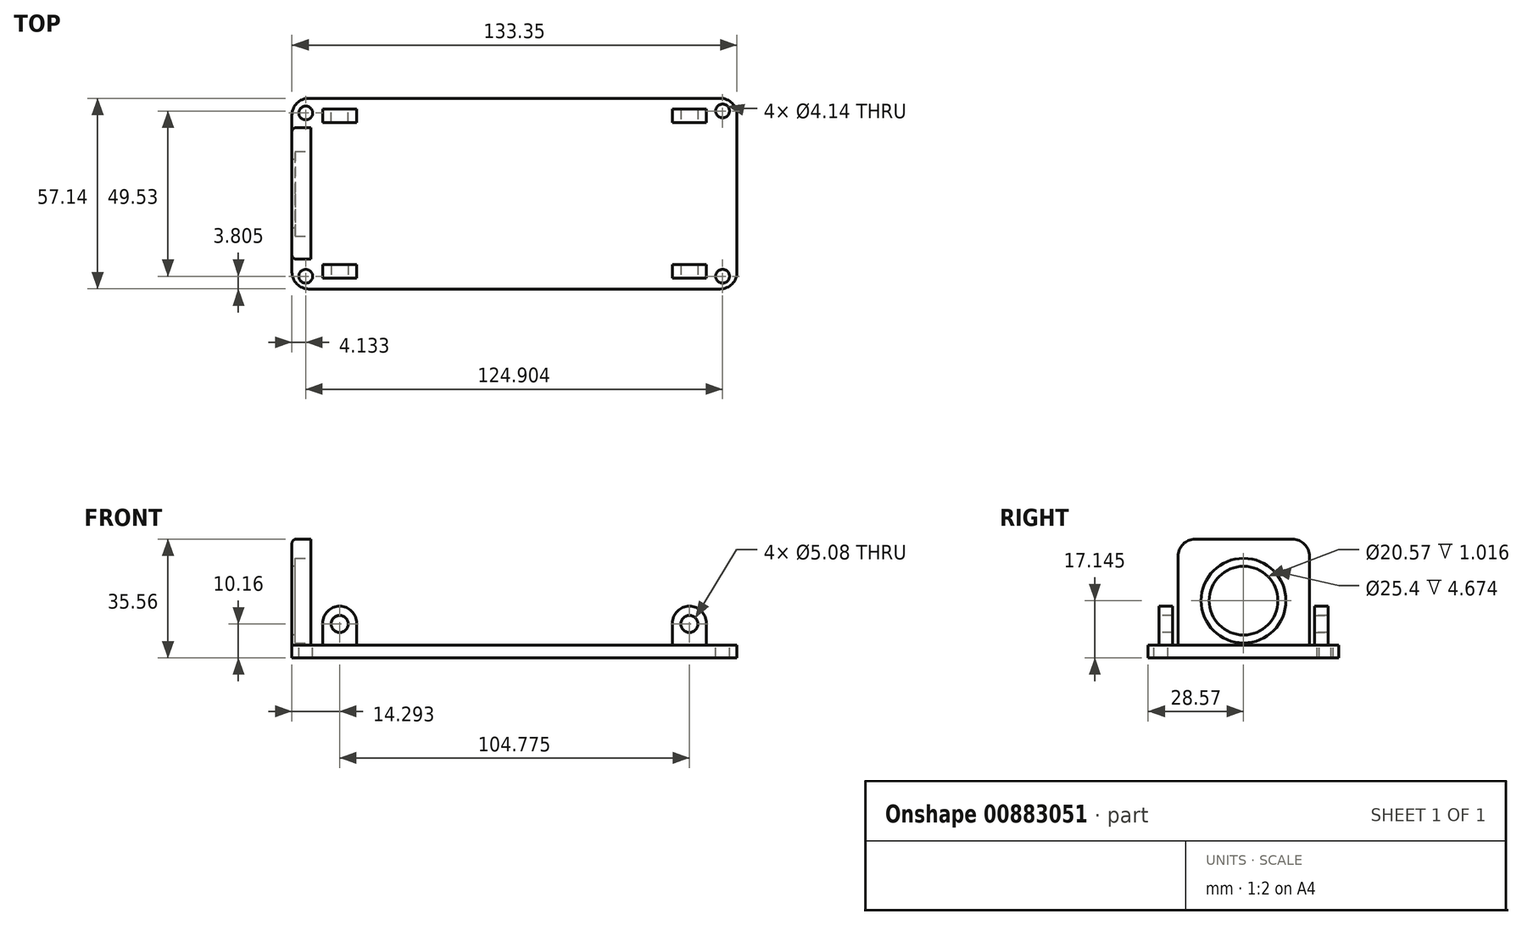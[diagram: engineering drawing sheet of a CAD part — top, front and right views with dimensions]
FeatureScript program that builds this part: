
annotation { "Feature Type Name" : "Feature", "Feature Type Description" : "" }
export const myFeature = defineFeature(function(context is Context, id is Id, definition is map)
    precondition{}
    {
        {
            var Q0;
            Q0=qCreatedBy(makeId("Top.planeOp"),FACE);
            var sketch = newSketch(context, id + "F0", { "sketchPlane" : qUnion([Q0])});
            skLineSegment(sketch, "E0.bottom", {"start": v(57.47, -25.34) * mm, "end": v(-57.47, -25.34) * mm});
            skLineSegment(sketch, "E0.top", {"start": v(57.47, 25.34) * mm, "end": v(-57.47, 25.34) * mm});
            skLineSegment(sketch, "E0.left", {"start": v(57.47, -25.34) * mm, "end": v(57.47, 25.34) * mm});
            skLineSegment(sketch, "E0.right", {"start": v(-57.47, -25.34) * mm, "end": v(-57.47, 25.34) * mm});
            skPoint(sketch, "E0.middle", {"position": v(0, 0) * mm});
            skPoint(sketch, "E1", {"position": v(-57.47, 25.34) * mm});
            skPoint(sketch, "E2", {"position": v(57.47, 25.34) * mm});
            skPoint(sketch, "E3", {"position": v(57.47, -25.34) * mm});
            skPoint(sketch, "E4", {"position": v(-57.47, -25.34) * mm});
            skLineSegment(sketch, "E5.bottom", {"start": v(-57.47, 25.34) * mm, "end": v(-47.3, 25.34) * mm});
            skLineSegment(sketch, "E5.top", {"start": v(-57.47, 21.27) * mm, "end": v(-47.3, 21.27) * mm});
            skLineSegment(sketch, "E5.left", {"start": v(-57.47, 25.34) * mm, "end": v(-57.47, 21.27) * mm});
            skLineSegment(sketch, "E5.right", {"start": v(-47.3, 25.34) * mm, "end": v(-47.3, 21.27) * mm});
            skLineSegment(sketch, "E6.bottom", {"start": v(-57.47, -25.34) * mm, "end": v(-47.3, -25.34) * mm});
            skLineSegment(sketch, "E6.top", {"start": v(-57.47, -21.27) * mm, "end": v(-47.3, -21.27) * mm});
            skLineSegment(sketch, "E6.left", {"start": v(-57.47, -25.34) * mm, "end": v(-57.47, -21.27) * mm});
            skLineSegment(sketch, "E6.right", {"start": v(-47.3, -25.34) * mm, "end": v(-47.3, -21.27) * mm});
            skLineSegment(sketch, "E7.bottom", {"start": v(57.47, 25.34) * mm, "end": v(47.3, 25.34) * mm});
            skLineSegment(sketch, "E7.top", {"start": v(57.47, 21.27) * mm, "end": v(47.3, 21.27) * mm});
            skLineSegment(sketch, "E7.left", {"start": v(57.47, 25.34) * mm, "end": v(57.47, 21.27) * mm});
            skLineSegment(sketch, "E7.right", {"start": v(47.3, 25.34) * mm, "end": v(47.3, 21.27) * mm});
            skLineSegment(sketch, "E8.bottom", {"start": v(57.47, -25.34) * mm, "end": v(47.3, -25.34) * mm});
            skLineSegment(sketch, "E8.top", {"start": v(57.47, -21.27) * mm, "end": v(47.3, -21.27) * mm});
            skLineSegment(sketch, "E8.left", {"start": v(57.47, -25.34) * mm, "end": v(57.47, -21.27) * mm});
            skLineSegment(sketch, "E8.right", {"start": v(47.3, -25.34) * mm, "end": v(47.3, -21.27) * mm});
            skLineSegment(sketch, "E9.bottom", {"start": v(-47.3, 21.27) * mm, "end": v(47.3, 21.27) * mm});
            skLineSegment(sketch, "E9.top", {"start": v(-47.3, -21.27) * mm, "end": v(47.3, -21.27) * mm});
            skLineSegment(sketch, "E9.left", {"start": v(-47.3, 21.27) * mm, "end": v(-47.3, -21.27) * mm});
            skLineSegment(sketch, "E9.right", {"start": v(47.3, 21.27) * mm, "end": v(47.3, -21.27) * mm});
            skLineSegment(sketch, "E10.bottom", {"start": v(66.68, -28.57) * mm, "end": v(-66.68, -28.58) * mm});
            skLineSegment(sketch, "E10.top", {"start": v(66.68, 28.58) * mm, "end": v(-66.68, 28.57) * mm});
            skLineSegment(sketch, "E10.left", {"start": v(66.68, -28.57) * mm, "end": v(66.68, 28.58) * mm});
            skLineSegment(sketch, "E10.right", {"start": v(-66.68, -28.58) * mm, "end": v(-66.68, 28.57) * mm});
            skSolve(sketch);
        }
        {
            var Q0;
            Q0=makeQuery(id+"F0.imprint","IMPRINT",FACE,{"disambiguationData":[TD([[makeQuery(id+"F0.imprint","IMPRINT",EDGE,{"derivedFrom":sQuery(id+"F0.wireOp",EDGE,"E10.bottom")}),-1.0]])]});
            var Q1;
            {var subQ2=sQuery(id+"F0.wireOp",EDGE,"E5.right");Q1=makeQuery(id+"F0.imprint","IMPRINT",FACE,{"disambiguationData":[TD([[makeQuery(id+"F0.imprint","IMPRINT",EDGE,{"derivedFrom":subQ2}),1.0]])]});}
            var Q2;
            {var subQ2=sQuery(id+"F0.wireOp",EDGE,"E5.top");Q2=makeQuery(id+"F0.imprint","IMPRINT",FACE,{"disambiguationData":[TD([[makeQuery(id+"F0.imprint","IMPRINT",EDGE,{"derivedFrom":subQ2}),-1.0]])]});}
            var Q3;
            {var subQ4=sQuery(id+"F0.wireOp",EDGE,"E6.top");Q3=makeQuery(id+"F0.imprint","IMPRINT",FACE,{"disambiguationData":[TD([[makeQuery(id+"F0.imprint","IMPRINT",EDGE,{"derivedFrom":subQ4}),-1.0]])]});}
            var Q4;
            {var subQ2=sQuery(id+"F0.wireOp",EDGE,"E6.right");Q4=makeQuery(id+"F0.imprint","IMPRINT",FACE,{"disambiguationData":[TD([[makeQuery(id+"F0.imprint","IMPRINT",EDGE,{"derivedFrom":subQ2}),-1.0]])]});}
            var Q5;
            Q5=makeQuery(id+"F0.imprint","IMPRINT",FACE,{"disambiguationData":[TD([[makeQuery(id+"F0.imprint","IMPRINT",EDGE,{"derivedFrom":sQuery(id+"F0.wireOp",EDGE,"E9.bottom")}),-1.0]])]});
            var Q6;
            {var subQ2=sQuery(id+"F0.wireOp",EDGE,"E7.top");Q6=makeQuery(id+"F0.imprint","IMPRINT",FACE,{"disambiguationData":[TD([[makeQuery(id+"F0.imprint","IMPRINT",EDGE,{"derivedFrom":subQ2}),1.0]])]});}
            var Q7;
            {var subQ4=sQuery(id+"F0.wireOp",EDGE,"E8.top");Q7=makeQuery(id+"F0.imprint","IMPRINT",FACE,{"disambiguationData":[TD([[makeQuery(id+"F0.imprint","IMPRINT",EDGE,{"derivedFrom":subQ4}),1.0]])]});}
            var Q8;
            {var subQ4=sQuery(id+"F0.wireOp",EDGE,"E7.top");Q8=makeQuery(id+"F0.imprint","IMPRINT",FACE,{"disambiguationData":[TD([[makeQuery(id+"F0.imprint","IMPRINT",EDGE,{"derivedFrom":subQ4}),-1.0]])]});}
            var Q9;
            {var subQ4=sQuery(id+"F0.wireOp",EDGE,"E5.top");Q9=makeQuery(id+"F0.imprint","IMPRINT",FACE,{"disambiguationData":[TD([[makeQuery(id+"F0.imprint","IMPRINT",EDGE,{"derivedFrom":subQ4}),1.0]])]});}
            extrude(context, id + "F1", {"entities" : qUnion([Q0, Q1, Q2, Q3, Q4, Q5, Q6, Q7, Q8, Q9]), "depth" : 3.8 * mm, "offsetDistance" : 25.4 * mm});
        }
        {
            var Q0;
            Q0=makeQuery(id+"F1.opExtrude","CAP_FACE",FACE,{"disambiguationData":[OSD([sQuery(id+"F0.wireOp",EDGE,"E10.bottom"),sQuery(id+"F0.wireOp",EDGE,"E10.top"),sQuery(id+"F0.wireOp",EDGE,"E10.left"),sQuery(id+"F0.wireOp",EDGE,"E10.right")])],"isStart":false});
            var sketch = newSketch(context, id + "F2", { "sketchPlane" : qUnion([Q0])});
            skLineSegment(sketch, "E11.bottom", {"start": v(-60.99, 19.75) * mm, "end": v(-66.68, 19.75) * mm});
            skLineSegment(sketch, "E11.top", {"start": v(-60.99, -19.62) * mm, "end": v(-66.68, -19.62) * mm});
            skLineSegment(sketch, "E11.left", {"start": v(-60.99, 19.75) * mm, "end": v(-60.99, -19.62) * mm});
            skLineSegment(sketch, "E11.right", {"start": v(-66.68, 19.75) * mm, "end": v(-66.67, -19.62) * mm});
            skSolve(sketch);
        }
        {
            var Q0;
            Q0=makeQuery(id+"F2.imprint","IMPRINT",FACE,{"disambiguationData":[TD([[makeQuery(id+"F2.imprint","IMPRINT",EDGE,{"derivedFrom":sQuery(id+"F2.wireOp",EDGE,"E11.bottom")}),1.0]])]});
            extrude(context, id + "F3", {"entities" : qUnion([Q0]), "operationType" : NewBodyOperationType.ADD, "depth" : 31.75 * mm, "offsetDistance" : 25.4 * mm});
        }
        {
            var Q0;
            Q0=makeQuery(id+"F3.opExtrude","CAP_EDGE",EDGE,{"disambiguationData":[OSD([sQuery(id+"F2.wireOp",EDGE,"E11.bottom")])],"isStart":false});
            var Q1;
            Q1=makeQuery(id+"F3.opExtrude","CAP_EDGE",EDGE,{"disambiguationData":[OSD([sQuery(id+"F2.wireOp",EDGE,"E11.top")])],"isStart":false});
            fillet(context, id + "F4", {"entities" : qUnion([Q0, Q1]), "radius" : 5.08 * mm, "tangentPropagation" : true, "allowEdgeOverflow" : false});
        }
        {
            var Q0;
            Q0=makeQuery(id+"F3.boolean.opBoolean","MERGE",FACE,{"derivedFrom":[makeQuery(id+"F1.opExtrude","SWEPT_FACE",FACE,{"disambiguationData":[OSD([sQuery(id+"F0.wireOp",EDGE,"E10.right")])]}),makeQuery(id+"F3.opExtrude","SWEPT_FACE",FACE,{"disambiguationData":[OSD([sQuery(id+"F2.wireOp",EDGE,"E11.right")])]})]});
            var sketch = newSketch(context, id + "F5", { "sketchPlane" : qUnion([Q0])});
            skCircle(sketch, "E12", {"center": v(0, 17.14) * mm, "radius": 10.29 * mm});
            skPoint(sketch, "E12.centerSnap0", {"position": v(-19.75, 17.14) * mm});
            skSolve(sketch);
        }
        {
            var Q0;
            Q0 = qSketchRegion(id + "F5", true);
            extrude(context, id + "F6", {"entities" : qUnion([Q0]), "operationType" : NewBodyOperationType.REMOVE, "oppositeDirection" : true, "depth" : 25.4 * mm, "offsetDistance" : 25.4 * mm});
        }
        {
            var Q0;
            Q0=makeQuery(id+"F1.opExtrude","CAP_FACE",FACE,{"disambiguationData":[OSD([sQuery(id+"F0.wireOp",EDGE,"E10.bottom"),sQuery(id+"F0.wireOp",EDGE,"E10.top"),sQuery(id+"F0.wireOp",EDGE,"E10.left"),sQuery(id+"F0.wireOp",EDGE,"E10.right")])],"isStart":false});
            var sketch = newSketch(context, id + "F7", { "sketchPlane" : qUnion([Q0])});
            skLineSegment(sketch, "E13.left", {"start": v(-66.68, 28.57) * mm, "end": v(-66.68, 22.39) * mm});
            skCircle(sketch, "E14", {"center": v(-62.55, 24.16) * mm, "radius": 2.07 * mm});
            skCircle(sketch, "E15", {"center": v(62.36, 24.76) * mm, "radius": 2.07 * mm});
            skLineSegment(sketch, "E16.top", {"start": v(66.68, -22.99) * mm, "end": v(56.52, -22.99) * mm});
            skLineSegment(sketch, "E16.left", {"start": v(66.68, -28.57) * mm, "end": v(66.68, -22.99) * mm});
            skCircle(sketch, "E17", {"center": v(-62.55, -24.76) * mm, "radius": 2.07 * mm});
            skCircle(sketch, "E18", {"center": v(62.36, -24.77) * mm, "radius": 2.07 * mm});
            skSolve(sketch);
        }
        {
            var Q0;
            Q0 = qSketchRegion(id + "F7", true);
            extrude(context, id + "F8", {"entities" : qUnion([Q0]), "operationType" : NewBodyOperationType.REMOVE, "endBound" : BoundingType.THROUGH_ALL, "oppositeDirection" : true, "depth" : 25.4 * mm, "offsetDistance" : 25.4 * mm});
        }
        {
            var Q0;
            Q0=makeQuery(id+"F1.opExtrude","SWEPT_EDGE",EDGE,{"disambiguationData":[OSD([sQuery(id+"F0.wireOp",EDGE,"E10.top"),sQuery(id+"F0.wireOp",EDGE,"E10.left")])]});
            var Q1;
            Q1=makeQuery(id+"F1.opExtrude","SWEPT_EDGE",EDGE,{"disambiguationData":[OSD([sQuery(id+"F0.wireOp",EDGE,"E10.top"),sQuery(id+"F0.wireOp",EDGE,"E10.right")])]});
            var Q2;
            Q2=makeQuery(id+"F1.opExtrude","SWEPT_EDGE",EDGE,{"disambiguationData":[OSD([sQuery(id+"F0.wireOp",EDGE,"E10.bottom"),sQuery(id+"F0.wireOp",EDGE,"E10.right")])]});
            var Q3;
            Q3=makeQuery(id+"F1.opExtrude","SWEPT_EDGE",EDGE,{"disambiguationData":[OSD([sQuery(id+"F0.wireOp",EDGE,"E10.bottom"),sQuery(id+"F0.wireOp",EDGE,"E10.left")])]});
            fillet(context, id + "F9", {"entities" : qUnion([Q0, Q1, Q2, Q3]), "radius" : 5.08 * mm, "tangentPropagation" : true, "allowEdgeOverflow" : false});
        }
        {
            var Q0;
            Q0=makeQuery(id+"F3.opExtrude","CAP_EDGE",EDGE,{"disambiguationData":[OSD([sQuery(id+"F2.wireOp",EDGE,"E11.right")])],"isStart":false});
            fillet(context, id + "F10", {"entities" : qUnion([Q0]), "radius" : 1.27 * mm, "tangentPropagation" : true, "allowEdgeOverflow" : false});
        }
        {
            var Q0;
            Q0=makeQuery(id+"F3.opExtrude","SWEPT_FACE",FACE,{"disambiguationData":[OSD([sQuery(id+"F2.wireOp",EDGE,"E11.left")])]});
            var sketch = newSketch(context, id + "F11", { "sketchPlane" : qUnion([Q0])});
            skCircle(sketch, "E19", {"center": v(0, 17.14) * mm, "radius": 12.7 * mm});
            skSolve(sketch);
        }
        {
            var Q0;
            Q0=makeQuery(id+"F11.imprint","IMPRINT",FACE,{"disambiguationData":[TD([[makeQuery(id+"F11.imprint","IMPRINT",EDGE,{"derivedFrom":sQuery(id+"F11.wireOp",EDGE,"E19")}),1.0]])]});
            var Q1;
            Q1=sQuery(id+"F11.wireOp",EDGE,"E19");
            extrude(context, id + "F12", {"entities" : qUnion([Q0]), "operationType" : NewBodyOperationType.REMOVE, "surfaceEntities" : qUnion([Q1]), "oppositeDirection" : true, "depth" : 4.67 * mm, "offsetDistance" : 25.4 * mm});
        }
        {
            var Q0;
            {var subQ4=sQuery(id+"F0.wireOp",EDGE,"E7.top");Q0=makeQuery(id+"F0.imprint","IMPRINT",FACE,{"disambiguationData":[TD([[makeQuery(id+"F0.imprint","IMPRINT",EDGE,{"derivedFrom":subQ4}),-1.0]])]});}
            var Q1;
            {var subQ4=sQuery(id+"F0.wireOp",EDGE,"E8.top");Q1=makeQuery(id+"F0.imprint","IMPRINT",FACE,{"disambiguationData":[TD([[makeQuery(id+"F0.imprint","IMPRINT",EDGE,{"derivedFrom":subQ4}),1.0]])]});}
            var Q2;
            {var subQ4=sQuery(id+"F0.wireOp",EDGE,"E5.top");Q2=makeQuery(id+"F0.imprint","IMPRINT",FACE,{"disambiguationData":[TD([[makeQuery(id+"F0.imprint","IMPRINT",EDGE,{"derivedFrom":subQ4}),1.0]])]});}
            var Q3;
            {var subQ4=sQuery(id+"F0.wireOp",EDGE,"E6.top");Q3=makeQuery(id+"F0.imprint","IMPRINT",FACE,{"disambiguationData":[TD([[makeQuery(id+"F0.imprint","IMPRINT",EDGE,{"derivedFrom":subQ4}),-1.0]])]});}
            var Q4;
            Q4=sQuery(id+"F0.wireOp",EDGE,"E7.top");
            var Q5;
            Q5=sQuery(id+"F0.wireOp",EDGE,"E7.right");
            var Q6;
            Q6=sQuery(id+"F0.wireOp",EDGE,"E7.bottom");
            var Q7;
            Q7=sQuery(id+"F0.wireOp",EDGE,"E7.left");
            extrude(context, id + "F13", {"entities" : qUnion([Q0, Q1, Q2, Q3]), "operationType" : NewBodyOperationType.ADD, "surfaceEntities" : qUnion([Q4, Q5, Q6, Q7]), "depth" : 15.5 * mm, "offsetDistance" : 25.4 * mm});
        }
        {
            var Q0;
            {var subQ0=sQuery(id+"F0.wireOp",EDGE,"E0.top");Q0=makeQuery(id+"F13.opExtrude","SWEPT_FACE",FACE,{"disambiguationData":[OSD([subQ0]),TDD([makeQuery(id+"F0.imprint","IMPRINT",EDGE,{"disambiguationData":[TD([[makeQuery(id+"F0.imprint","INTERSECT",VERTEX,{"derivedFrom":[subQ0,sQuery(id+"F0.wireOp",EDGE,"E0.right")]}),1.0]])],"derivedFrom":subQ0})])]});}
            var sketch = newSketch(context, id + "F14", { "sketchPlane" : qUnion([Q0])});
            skCircle(sketch, "E20", {"center": v(52.39, 10.16) * mm, "radius": 2.54 * mm});
            skPoint(sketch, "E20.centerSnap0", {"position": v(52.39, 15.5) * mm});
            skPoint(sketch, "E20.centerSnap1", {"position": v(57.47, 9.65) * mm});
            skSolve(sketch);
        }
        {
            var Q0;
            Q0=makeQuery(id+"F14.imprint","IMPRINT",FACE,{"disambiguationData":[TD([[makeQuery(id+"F14.imprint","IMPRINT",EDGE,{"derivedFrom":sQuery(id+"F14.wireOp",EDGE,"E20")}),1.0]])]});
            extrude(context, id + "F15", {"entities" : qUnion([Q0]), "operationType" : NewBodyOperationType.REMOVE, "oppositeDirection" : true, "depth" : 5.08 * mm, "offsetDistance" : 25.4 * mm});
        }
        {
            var Q0;
            {var subQ0=sQuery(id+"F0.wireOp",EDGE,"E0.bottom");Q0=makeQuery(id+"F13.opExtrude","SWEPT_FACE",FACE,{"disambiguationData":[OSD([subQ0]),TDD([makeQuery(id+"F0.imprint","IMPRINT",EDGE,{"disambiguationData":[TD([[makeQuery(id+"F0.imprint","INTERSECT",VERTEX,{"derivedFrom":[subQ0,sQuery(id+"F0.wireOp",EDGE,"E8.right")]}),1.0]])],"derivedFrom":subQ0})])]});}
            var sketch = newSketch(context, id + "F16", { "sketchPlane" : qUnion([Q0])});
            skCircle(sketch, "E21", {"center": v(52.39, 10.16) * mm, "radius": 2.54 * mm});
            skPoint(sketch, "E21.centerSnap0", {"position": v(52.39, 15.5) * mm});
            skPoint(sketch, "E21.centerSnap1", {"position": v(57.47, 9.65) * mm});
            skSolve(sketch);
        }
        {
            var Q0;
            Q0 = qSketchRegion(id + "F16", true);
            extrude(context, id + "F17", {"entities" : qUnion([Q0]), "operationType" : NewBodyOperationType.REMOVE, "oppositeDirection" : true, "depth" : 25.4 * mm, "offsetDistance" : 25.4 * mm});
        }
        {
            var Q0;
            Q0=makeQuery(id+"F13.opExtrude","SWEPT_FACE",FACE,{"disambiguationData":[OSD([sQuery(id+"F0.wireOp",EDGE,"E7.top")])]});
            var sketch = newSketch(context, id + "F18", { "sketchPlane" : qUnion([Q0])});
            skCircle(sketch, "E22", {"center": v(52.39, 10.16) * mm, "radius": 2.54 * mm});
            skPoint(sketch, "E22.centerSnap0", {"position": v(52.39, 15.5) * mm});
            skPoint(sketch, "E22.centerSnap1", {"position": v(57.47, 9.65) * mm});
            skSolve(sketch);
        }
        {
            var Q0;
            Q0 = qSketchRegion(id + "F18", true);
            extrude(context, id + "F19", {"entities" : qUnion([Q0]), "operationType" : NewBodyOperationType.REMOVE, "oppositeDirection" : true, "depth" : 25.4 * mm, "offsetDistance" : 25.4 * mm});
        }
        {
            var Q0;
            {var subQ0=sQuery(id+"F0.wireOp",EDGE,"E0.bottom");Q0=makeQuery(id+"F13.opExtrude","SWEPT_FACE",FACE,{"disambiguationData":[OSD([subQ0]),TDD([makeQuery(id+"F0.imprint","IMPRINT",EDGE,{"disambiguationData":[TD([[makeQuery(id+"F0.imprint","INTERSECT",VERTEX,{"derivedFrom":[subQ0,sQuery(id+"F0.wireOp",EDGE,"E6.right")]}),-1.0]])],"derivedFrom":subQ0})])]});}
            var sketch = newSketch(context, id + "F20", { "sketchPlane" : qUnion([Q0])});
            skCircle(sketch, "E23", {"center": v(-52.39, 10.16) * mm, "radius": 2.54 * mm});
            skPoint(sketch, "E23.centerSnap0", {"position": v(-52.39, 15.5) * mm});
            skPoint(sketch, "E23.centerSnap1", {"position": v(-47.3, 9.65) * mm});
            skSolve(sketch);
        }
        {
            var Q0;
            Q0 = qSketchRegion(id + "F20", true);
            extrude(context, id + "F21", {"entities" : qUnion([Q0]), "operationType" : NewBodyOperationType.REMOVE, "oppositeDirection" : true, "depth" : 25.4 * mm, "offsetDistance" : 25.4 * mm});
        }
        {
            var Q0;
            Q0=makeQuery(id+"F13.opExtrude","CAP_EDGE",EDGE,{"disambiguationData":[OSD([sQuery(id+"F0.wireOp",EDGE,"E6.right")])],"isStart":false});
            var Q1;
            {var subQ0=sQuery(id+"F0.wireOp",EDGE,"E0.right");Q1=makeQuery(id+"F13.opExtrude","CAP_EDGE",EDGE,{"disambiguationData":[OSD([subQ0]),TDD([makeQuery(id+"F0.imprint","IMPRINT",EDGE,{"disambiguationData":[TD([[makeQuery(id+"F0.imprint","INTERSECT",VERTEX,{"derivedFrom":[subQ0,sQuery(id+"F0.wireOp",EDGE,"E6.top")]}),1.0]])],"derivedFrom":subQ0})])],"isStart":false});}
            var Q2;
            {var subQ0=sQuery(id+"F0.wireOp",EDGE,"E0.right");Q2=makeQuery(id+"F13.opExtrude","CAP_EDGE",EDGE,{"disambiguationData":[OSD([subQ0]),TDD([makeQuery(id+"F0.imprint","IMPRINT",EDGE,{"disambiguationData":[TD([[makeQuery(id+"F0.imprint","INTERSECT",VERTEX,{"derivedFrom":[sQuery(id+"F0.wireOp",EDGE,"E0.top"),subQ0]}),1.0]])],"derivedFrom":subQ0})])],"isStart":false});}
            var Q3;
            Q3=makeQuery(id+"F13.opExtrude","CAP_EDGE",EDGE,{"disambiguationData":[OSD([sQuery(id+"F0.wireOp",EDGE,"E5.right")])],"isStart":false});
            var Q4;
            Q4=makeQuery(id+"F13.opExtrude","CAP_EDGE",EDGE,{"disambiguationData":[OSD([sQuery(id+"F0.wireOp",EDGE,"E7.right")])],"isStart":false});
            var Q5;
            Q5=makeQuery(id+"F13.opExtrude","CAP_EDGE",EDGE,{"disambiguationData":[OSD([sQuery(id+"F0.wireOp",EDGE,"E8.right")])],"isStart":false});
            var Q6;
            {var subQ0=sQuery(id+"F0.wireOp",EDGE,"E0.left");Q6=makeQuery(id+"F13.opExtrude","CAP_EDGE",EDGE,{"disambiguationData":[OSD([subQ0]),TDD([makeQuery(id+"F0.imprint","IMPRINT",EDGE,{"disambiguationData":[TD([[makeQuery(id+"F0.imprint","INTERSECT",VERTEX,{"derivedFrom":[subQ0,sQuery(id+"F0.wireOp",EDGE,"E8.top")]}),1.0]])],"derivedFrom":subQ0})])],"isStart":false});}
            var Q7;
            {var subQ0=sQuery(id+"F0.wireOp",EDGE,"E0.left");Q7=makeQuery(id+"F13.opExtrude","CAP_EDGE",EDGE,{"disambiguationData":[OSD([subQ0]),TDD([makeQuery(id+"F0.imprint","IMPRINT",EDGE,{"disambiguationData":[TD([[makeQuery(id+"F0.imprint","INTERSECT",VERTEX,{"derivedFrom":[subQ0,sQuery(id+"F0.wireOp",EDGE,"E7.top")]}),-1.0]])],"derivedFrom":subQ0})])],"isStart":false});}
            fillet(context, id + "F22", {"entities" : qUnion([Q0, Q1, Q2, Q3, Q4, Q5, Q6, Q7]), "radius" : 5.08 * mm, "tangentPropagation" : true, "allowEdgeOverflow" : false});
        }
    });
